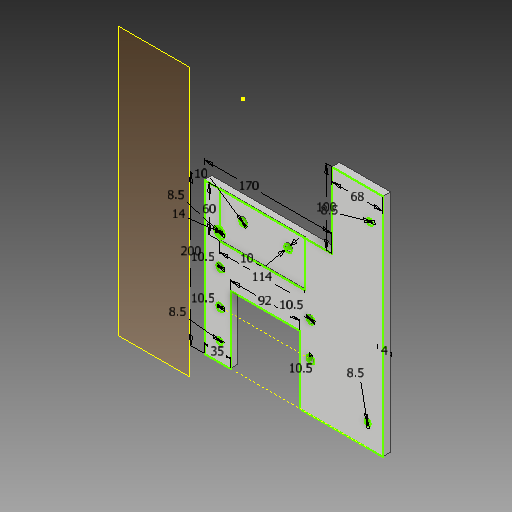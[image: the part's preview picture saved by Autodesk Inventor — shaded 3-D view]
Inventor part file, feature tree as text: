
AUTODESK INVENTOR PART (.ipt)
format: ipt  version: 2018 (Build 220112000, 112)  size: 158,720 bytes
history: native  units: mm
features: extrude x5, plane x1, sketch x1
ambient origin geometry x8: Origin, YZ Plane, XZ Plane, XY Plane, X Axis, Y Axis, Z Axis, Center Point
bodies: Body1 (feature_tree)
feature tree (7):
  plane  "Work Plane1"
  sketch  "Sketch1"  dims[d52=8.5mm d57=10.0mm d59=10.0mm d61=35.0mm d62=92.0mm d70=8.5mm d71=8.5mm d72=4.0mm d73=68.0mm d75=8.5mm d76=100.0mm d77=200.0mm d78=170.0mm d80=60.0mm d81=114.0mm d82=10.0mm d83=0.0mm d84=10.0mm d85=0.0mm d86=1.5mm d87=0.0mm d88=14.0mm d89=1.5mm d90=0.0mm d95=10.5mm d96=10.5mm d100=10.5mm d101=10.5mm d102=10.5mm d103=0.0mm]
  extrude  "Extrusion5"  Depth=10.0mm
  extrude  "Extrusion7"  Depth=10.0mm
  extrude  "Extrusion6"  Depth=35.0mm
  extrude  "Extrusion8"  Depth=92.0mm
  extrude  "Extrusion9"  Depth=8.5mm
